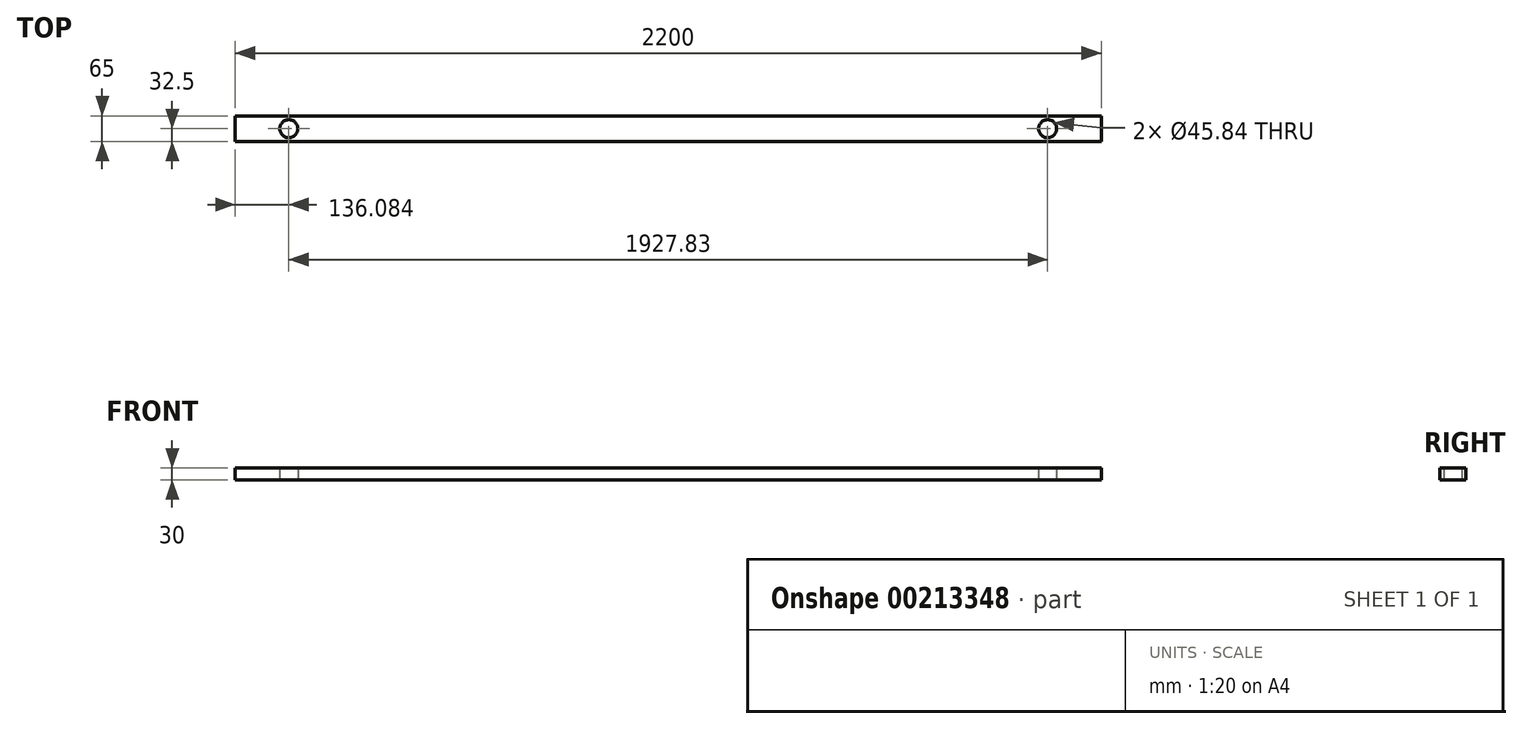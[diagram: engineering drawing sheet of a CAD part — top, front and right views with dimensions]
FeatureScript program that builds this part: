
annotation { "Feature Type Name" : "Feature", "Feature Type Description" : "" }
export const myFeature = defineFeature(function(context is Context, id is Id, definition is map)
    precondition{}
    {
        {
            var Q0;
            Q0=qCreatedBy(makeId("Top.planeOp"),FACE);
            var sketch = newSketch(context, id + "F0", { "sketchPlane" : qUnion([Q0])});
            skLineSegment(sketch, "E0.bottom", {"start": v(1100, 32.5) * mm, "end": v(-1100, 32.5) * mm});
            skLineSegment(sketch, "E0.top", {"start": v(1100, -32.5) * mm, "end": v(-1100, -32.5) * mm});
            skLineSegment(sketch, "E0.left", {"start": v(1100, 32.5) * mm, "end": v(1100, -32.5) * mm});
            skLineSegment(sketch, "E0.right", {"start": v(-1100, 32.5) * mm, "end": v(-1100, -32.5) * mm});
            skPoint(sketch, "E0.middle", {"position": v(0, 0) * mm});
            skCircle(sketch, "E1", {"center": v(-963.92, 0) * mm, "radius": 22.92 * mm});
            skCircle(sketch, "E2.MirrorC", {"center": v(963.92, 0) * mm, "radius": 22.92 * mm});
            skSolve(sketch);
        }
        {
            var Q0;
            Q0=makeQuery(id+"F0.imprint","IMPRINT",FACE,{"disambiguationData":[TD([[makeQuery(id+"F0.imprint","IMPRINT",EDGE,{"derivedFrom":sQuery(id+"F0.wireOp",EDGE,"E0.bottom")}),1.0]])]});
            extrude(context, id + "F1", {"entities" : qUnion([Q0]), "depth" : 30 * mm});
        }
    });
